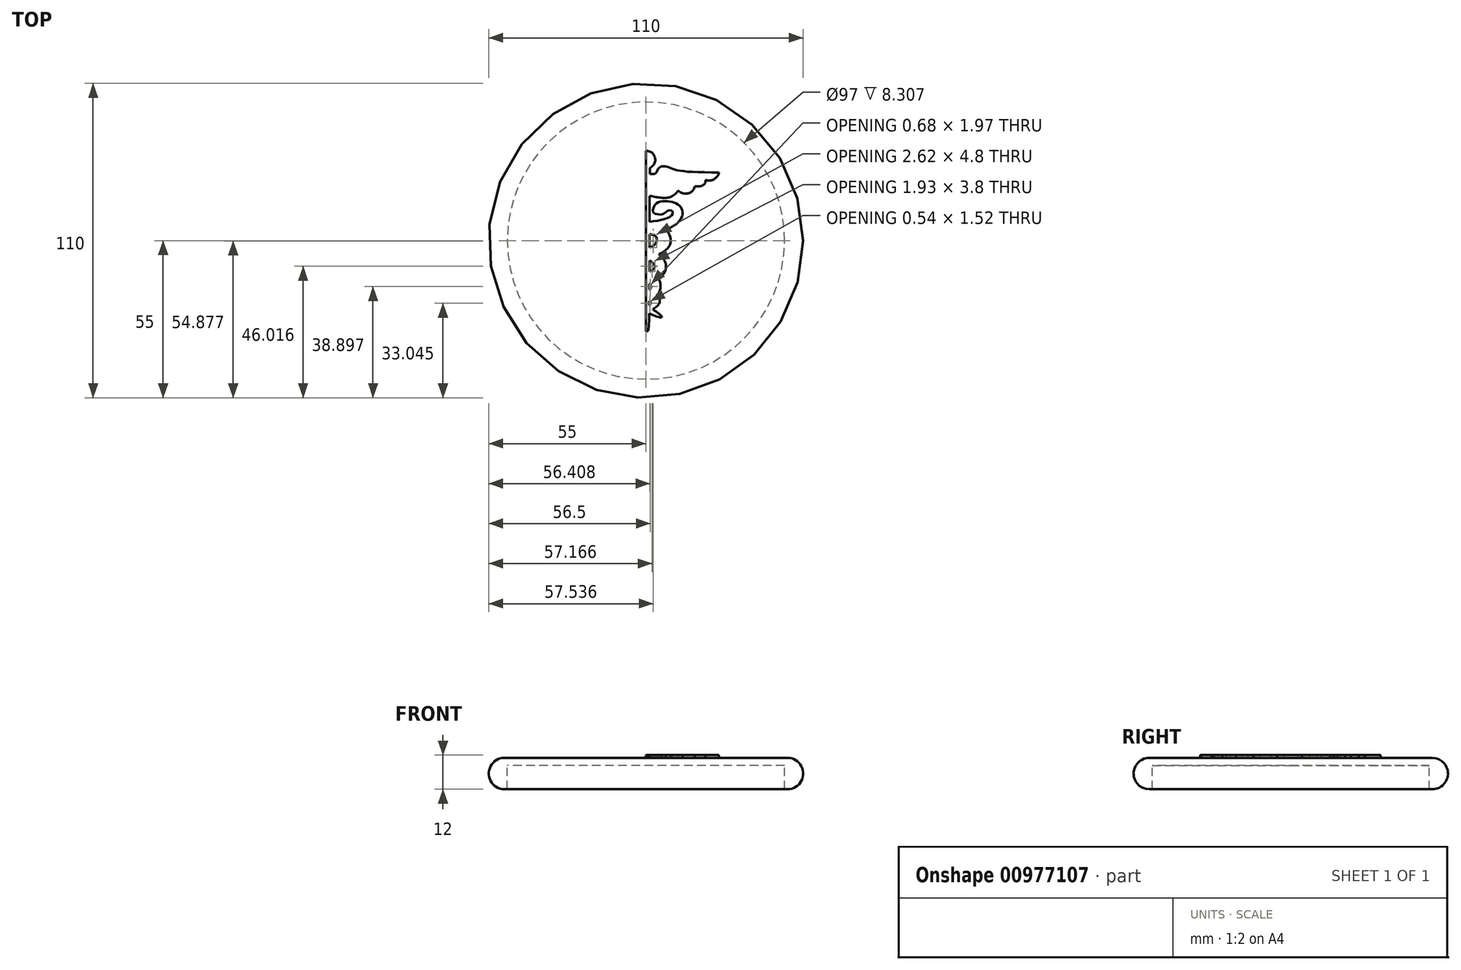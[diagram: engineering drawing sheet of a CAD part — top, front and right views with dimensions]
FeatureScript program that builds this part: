
annotation { "Feature Type Name" : "Feature", "Feature Type Description" : "" }
export const myFeature = defineFeature(function(context is Context, id is Id, definition is map)
    precondition{}
    {
        {
            var Q0;
            Q0=qCreatedBy(makeId("Front.planeOp"),FACE);
            var sketch = newSketch(context, id + "F0", { "sketchPlane" : qUnion([Q0])});
            skLineSegment(sketch, "E0", {"start": v(0, 11) * mm, "end": v(-49.5, 11) * mm});
            skLineSegment(sketch, "E1", {"start": v(-55, 0) * mm, "end": v(-55, 11) * mm, "construction": true});
            skLineSegment(sketch, "E2", {"start": v(0, 11) * mm, "end": v(0, 8.3) * mm});
            skLineSegment(sketch, "E3", {"start": v(0, 8.3) * mm, "end": v(-48.5, 8.3) * mm});
            skLineSegment(sketch, "E4", {"start": v(-48.5, 8.3) * mm, "end": v(-48.5, 0) * mm});
            skLineSegment(sketch, "E5", {"start": v(-48.5, 0) * mm, "end": v(-49.5, 0) * mm});
            skArc(sketch, "E6", {"start": v(-49.5, 11) * mm, "mid": v(-55, 5.5) * mm, "end": v(-49.5, 0) * mm});
            skLineSegment(sketch, "E7", {"start": v(-49.5, 11) * mm, "end": v(-55, 11) * mm, "construction": true});
            skLineSegment(sketch, "E8", {"start": v(-49.5, 0) * mm, "end": v(-55, 0) * mm, "construction": true});
            skSolve(sketch);
        }
        {
            var Q0;
            Q0 = qSketchRegion(id + "F0", true);
            var Q1;
            Q1=sQuery(id+"F0.wireOp",EDGE,"E2");
            revolve(context, id + "F1", {"surfaceOperationType" : NewSurfaceOperationType.NEW, "entities" : qUnion([Q0]), "axis" : qUnion([Q1]), "revolveType" : RevolveType.FULL});
        }
        {
            var Q0;
            Q0=makeQuery(id+"F1.opRevolve","SWEPT_FACE",FACE,{"disambiguationData":[OSD([sQuery(id+"F0.wireOp",EDGE,"E0")])]});
            var sketch = newSketch(context, id + "F2", { "sketchPlane" : qUnion([Q0])});
            skLineSegment(sketch, "E9", {"start": v(0, 110) * mm, "end": v(0, 63.77) * mm, "construction": true});
            skLineSegment(sketch, "E10", {"start": v(0, 63.77) * mm, "end": v(0, 63.05) * mm, "construction": true});
            skLineSegment(sketch, "E11", {"start": v(0, -63.77) * mm, "end": v(0, -110) * mm, "construction": true});
            skFitSpline(sketch, "E12", {"points": [v(0, 63.05) * mm, v(3.3, 62.22) * mm, v(5.64, 59.75) * mm, v(6.48, 56.18) * mm, v(5.32, 53.13) * mm, v(2.72, 50.95) * mm], "startDerivative": vector(17.59, -2.33) * mm, "endDerivative": vector(-14.12, -9.9) * mm});
            skLineSegment(sketch, "E13", {"start": v(2.72, 50.95) * mm, "end": v(2.72, 46.65) * mm});
            skLineSegment(sketch, "E14", {"start": v(2.72, 46.65) * mm, "end": v(5, 46.65) * mm});
            skFitSpline(sketch, "E15", {"points": [v(5, 46.65) * mm, v(6.8, 47.26) * mm, v(8.25, 49.97) * mm, v(10.46, 51.92) * mm, v(14.1, 52) * mm, v(17.87, 50.73) * mm, v(22.87, 49.2) * mm, v(51.09, 47.87) * mm], "startDerivative": vector(23.48, 2.78) * mm, "endDerivative": vector(130.72, 0.35) * mm});
            skFitSpline(sketch, "E16", {"points": [v(51.09, 47.87) * mm, v(49.97, 45.15) * mm, v(46.82, 42.68) * mm, v(43.76, 42.19) * mm, v(41.6, 42.57) * mm], "startDerivative": vector(-2.95, -11.25) * mm, "endDerivative": vector(-9.42, 2.45) * mm});
            skFitSpline(sketch, "E17", {"points": [v(41.6, 42.57) * mm, v(41.6, 41.48) * mm, v(40.98, 39.79) * mm, v(39.53, 38.72) * mm, v(37.94, 38.18) * mm, v(34.24, 38.22) * mm], "startDerivative": vector(0.73, -7.59) * mm, "endDerivative": vector(-14.95, 0.93) * mm});
            skFitSpline(sketch, "E18", {"points": [v(34.24, 38.22) * mm, v(33.34, 36.08) * mm, v(31.56, 34.06) * mm, v(28.78, 33.11) * mm, v(25.92, 33.25) * mm, v(22.25, 35.14) * mm], "startDerivative": vector(-4.26, -12.14) * mm, "endDerivative": vector(-15.86, 9.82) * mm});
            skFitSpline(sketch, "E19", {"points": [v(22.25, 35.14) * mm, v(21.17, 33.43) * mm, v(18.44, 31.33) * mm, v(15.26, 30.17) * mm, v(9.97, 30.22) * mm, v(3.92, 31.22) * mm], "startDerivative": vector(-5.97, -11.77) * mm, "endDerivative": vector(-27.18, 7.44) * mm});
            skLineSegment(sketch, "E20", {"start": v(3.92, 31.22) * mm, "end": v(2.6, 31.22) * mm});
            skLineSegment(sketch, "E21", {"start": v(2.6, 31.22) * mm, "end": v(2.53, 13.36) * mm});
            skLineSegment(sketch, "E22", {"start": v(2.23, -55.3) * mm, "end": v(1.61, -62.48) * mm});
            skFitSpline(sketch, "E23", {"points": [v(1.61, -62.48) * mm, v(1.23, -63.03) * mm, v(0.85, -63.25) * mm, v(0, -63.36) * mm], "startDerivative": vector(-1, -1.75) * mm, "endDerivative": vector(-2.54, -0.05) * mm});
            skFitSpline(sketch, "E24", {"points": [v(10.13, 27.6) * mm, v(8.03, 26.72) * mm, v(6.18, 25) * mm, v(4.92, 21.68) * mm, v(5.3, 19.68) * mm, v(8.18, 18.55) * mm, v(11.5, 18.57) * mm, v(14.12, 20.06) * mm, v(15.58, 21.2) * mm, v(17.87, 21.2) * mm, v(18.47, 20.84) * mm, v(18.66, 18.76) * mm, v(16.93, 16.9) * mm, v(9.88, 14.39) * mm, v(2.53, 13.36) * mm], "startDerivative": vector(-34.26, -11.96) * mm, "endDerivative": vector(-62.83, -5.66) * mm});
            skFitSpline(sketch, "E25", {"points": [v(10.13, 27.6) * mm, v(15.26, 27.6) * mm, v(20.39, 26.51) * mm, v(23.7, 24.47) * mm, v(25.38, 21.38) * mm, v(25.38, 17.62) * mm, v(22.57, 13.03) * mm, v(16.4, 8.85) * mm, v(8.9, 6.31) * mm, v(2.5, 5.58) * mm], "startDerivative": vector(46.45, 1.96) * mm, "endDerivative": vector(-51.3, -3.38) * mm});
            skLineSegment(sketch, "E26", {"start": v(14.27, 7.93) * mm, "end": v(14.27, 7.93) * mm});
            skFitSpline(sketch, "E27", {"points": [v(2.45, -4.9) * mm, v(4.8, -3.58) * mm, v(6.97, -1.5) * mm, v(7.68, 0.98) * mm, v(6.65, 3.26) * mm, v(5.18, 4.1) * mm, v(2.5, 4.7) * mm], "startDerivative": vector(13.6, 6.89) * mm, "endDerivative": vector(-16.6, 3.31) * mm});
            skLineSegment(sketch, "E28", {"start": v(9, -9.47) * mm, "end": v(9, -9.47) * mm});
            skLineSegment(sketch, "E29", {"start": v(2.4, -14.02) * mm, "end": v(2.4, -14.02) * mm});
            skFitSpline(sketch, "E30", {"points": [v(2.32, -34.03) * mm, v(3.45, -32.99) * mm, v(3.45, -30.92) * mm, v(2.34, -30.08) * mm], "startDerivative": vector(3.96, 2.13) * mm, "endDerivative": vector(-3.99, 1.96) * mm});
            skFitSpline(sketch, "E31", {"points": [v(8.32, -25.78) * mm, v(9.18, -27.1) * mm, v(9.92, -29.09) * mm, v(10.2, -31.88) * mm, v(9.18, -36.24) * mm, v(7.12, -38.43) * mm, v(4.59, -39.8) * mm, v(2.3, -40.48) * mm], "startDerivative": vector(8.16, -11.3) * mm, "endDerivative": vector(-16.65, -4.13) * mm});
            skFitSpline(sketch, "E32", {"points": [v(2.29, -42.24) * mm, v(3.2, -43.1) * mm, v(3.2, -44.2) * mm, v(2.27, -45.28) * mm], "startDerivative": vector(1.53, -1) * mm, "endDerivative": vector(-1.52, -1.8) * mm});
            skFitSpline(sketch, "E33", {"points": [v(7.47, -38.18) * mm, v(8.8, -39.13) * mm, v(9.56, -40.48) * mm, v(9.5, -43.07) * mm, v(7.62, -45.87) * mm, v(2.26, -48.98) * mm], "startDerivative": vector(10.72, -6.5) * mm, "endDerivative": vector(-12.62, -5.36) * mm});
            skLineSegment(sketch, "E34", {"start": v(4.67, -47.79) * mm, "end": v(4.67, -47.79) * mm});
            skLineSegment(sketch, "E35", {"start": v(0, 63.05) * mm, "end": v(0, -63.36) * mm});
            skLineSegment(sketch, "E36", {"start": v(0, -63.36) * mm, "end": v(0, -63.77) * mm, "construction": true});
            skFitSpline(sketch, "E37", {"points": [v(4.67, -47.79) * mm, v(6.05, -48.9) * mm, v(8.4, -50.54) * mm, v(10.02, -51.98) * mm, v(11.12, -53.08) * mm, v(10.86, -53.57) * mm, v(9.75, -53.62) * mm, v(2.25, -50.87) * mm], "startDerivative": vector(9.57, -7.92) * mm, "endDerivative": vector(-33.04, 13.47) * mm});
            skLineSegment(sketch, "E38", {"start": v(2.25, -50.87) * mm, "end": v(2.23, -55.3) * mm});
            skLineSegment(sketch, "E39", {"start": v(2.26, -48.98) * mm, "end": v(2.26, -48.98) * mm});
            skLineSegment(sketch, "E40", {"start": v(2.29, -42.24) * mm, "end": v(2.27, -45.28) * mm});
            skLineSegment(sketch, "E41", {"start": v(2.34, -30.08) * mm, "end": v(2.32, -34.03) * mm});
            skFitSpline(sketch, "E42", {"points": [v(2.4, -14.02) * mm, v(4.59, -15.3) * mm, v(5.87, -16.81) * mm, v(6.26, -17.75) * mm, v(5.9, -19.06) * mm, v(4.59, -20.28) * mm, v(2.38, -21.63) * mm], "startDerivative": vector(11.81, -5.81) * mm, "endDerivative": vector(-11.62, -6.84) * mm});
            skLineSegment(sketch, "E43", {"start": v(2.5, 4.7) * mm, "end": v(2.45, -4.9) * mm});
            skFitSpline(sketch, "E44", {"points": [v(14.27, 7.93) * mm, v(15.6, 5.73) * mm, v(17.06, 2.17) * mm, v(16.8, -2.53) * mm, v(13.28, -6.96) * mm, v(5.94, -10.79) * mm, v(2.42, -11.92) * mm], "startDerivative": vector(10.54, -16.76) * mm, "endDerivative": vector(-20.88, -5.9) * mm});
            skLineSegment(sketch, "E45", {"start": v(2.4, -21.61) * mm, "end": v(2.4, -21.61) * mm});
            skFitSpline(sketch, "E46", {"points": [v(9, -9.47) * mm, v(10.5, -10.81) * mm, v(13.04, -13.89) * mm, v(14, -17.14) * mm, v(12.97, -22.18) * mm, v(9.5, -25.23) * mm, v(2.35, -27.95) * mm], "startDerivative": vector(12.18, -10.23) * mm, "endDerivative": vector(-34.74, -11.6) * mm});
            skLineSegment(sketch, "E47", {"start": v(2.4, -14.02) * mm, "end": v(2.4, -21.61) * mm});
            skLineSegment(sketch, "E48", {"start": v(-35.77, -0.15) * mm, "end": v(0, -0.15) * mm, "construction": true});
            skSolve(sketch);
        }
        {
            var Q0;
            Q0 = qSketchRegion(id + "F2", true);
            extrude(context, id + "F3", {"entities" : qUnion([Q0]), "depth" : 2 * mm, "offsetDistance" : 25 * mm});
        }
        {
            var Q0;
            Q0=makeQuery(id+"F3.opExtrude","SWEPT_BODY",BODY,{"disambiguationData":[OSD([sQuery(id+"F2.wireOp",EDGE,"E12"),sQuery(id+"F2.wireOp",EDGE,"E13"),sQuery(id+"F2.wireOp",EDGE,"E14"),sQuery(id+"F2.wireOp",EDGE,"E15"),sQuery(id+"F2.wireOp",EDGE,"E16"),sQuery(id+"F2.wireOp",EDGE,"E17"),sQuery(id+"F2.wireOp",EDGE,"E18"),sQuery(id+"F2.wireOp",EDGE,"E19"),sQuery(id+"F2.wireOp",EDGE,"E20"),sQuery(id+"F2.wireOp",EDGE,"E21"),sQuery(id+"F2.wireOp",EDGE,"E22"),sQuery(id+"F2.wireOp",EDGE,"E23"),sQuery(id+"F2.wireOp",EDGE,"E24"),sQuery(id+"F2.wireOp",EDGE,"E25"),sQuery(id+"F2.wireOp",EDGE,"E27"),sQuery(id+"F2.wireOp",EDGE,"E30"),sQuery(id+"F2.wireOp",EDGE,"E31"),sQuery(id+"F2.wireOp",EDGE,"E32"),sQuery(id+"F2.wireOp",EDGE,"E33"),sQuery(id+"F2.wireOp",EDGE,"E35"),sQuery(id+"F2.wireOp",EDGE,"E37"),sQuery(id+"F2.wireOp",EDGE,"E38"),sQuery(id+"F2.wireOp",EDGE,"E40"),sQuery(id+"F2.wireOp",EDGE,"E41"),sQuery(id+"F2.wireOp",EDGE,"E42"),sQuery(id+"F2.wireOp",EDGE,"E43"),sQuery(id+"F2.wireOp",EDGE,"E44"),sQuery(id+"F2.wireOp",EDGE,"E46"),sQuery(id+"F2.wireOp",EDGE,"E47")])]});
            var Q1;
            Q1=sQuery(id+"F2.wireOp",VERTEX,"E48.end");
            transform(context, id + "F4", {"entities" : qUnion([Q0]), "transformType" : TransformType.SCALE_UNIFORMLY, "scale" : .5, "scalePoint" : qUnion([Q1]), "makeCopy" : false});
        }
    });
